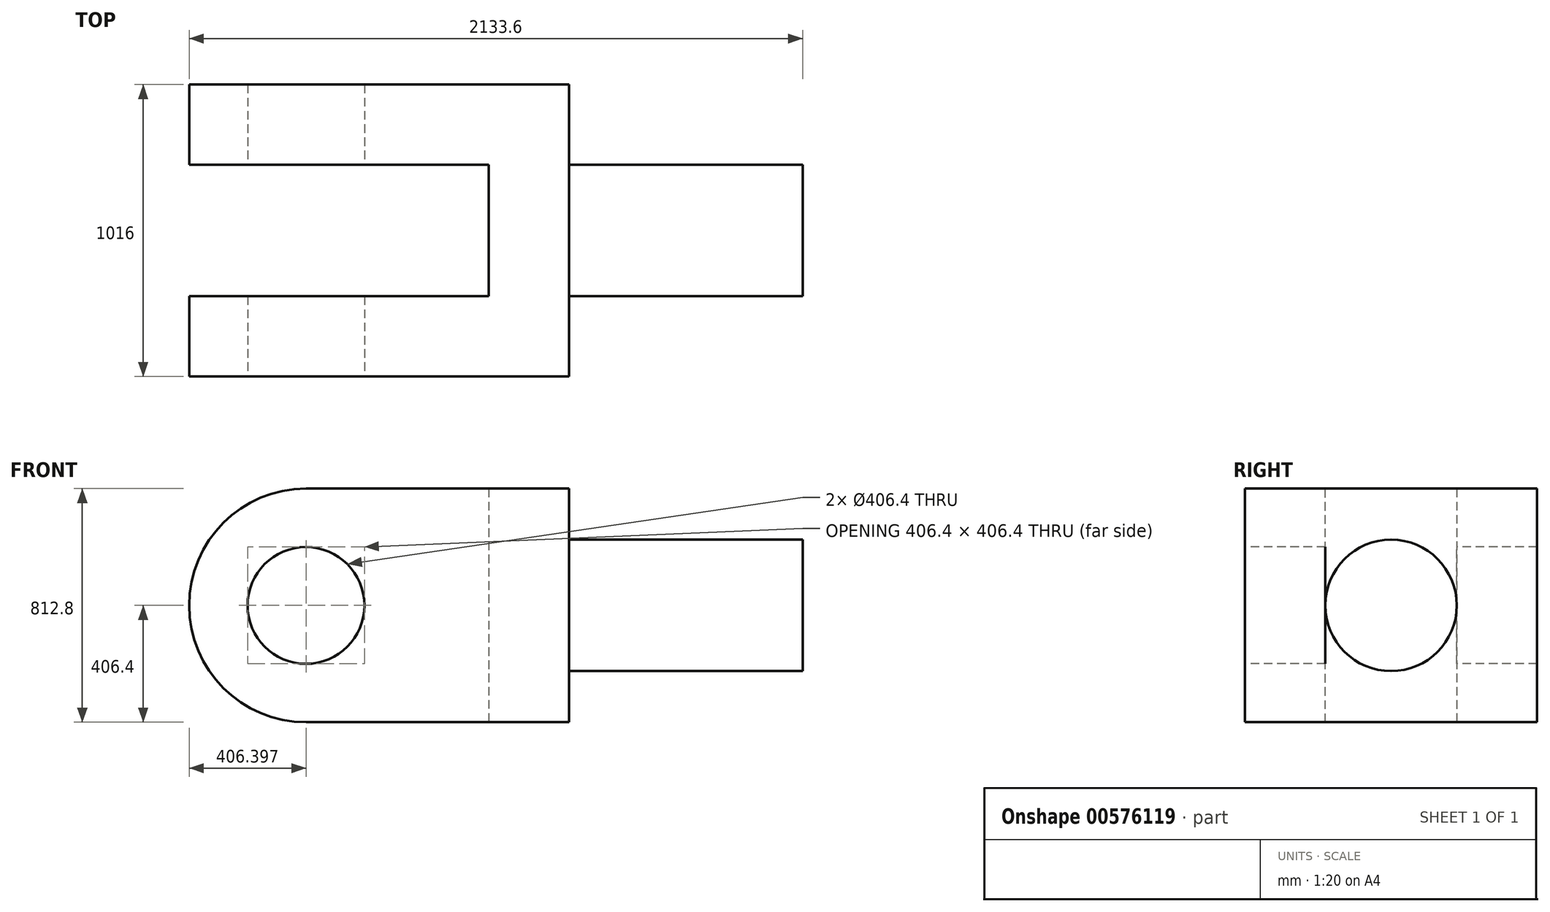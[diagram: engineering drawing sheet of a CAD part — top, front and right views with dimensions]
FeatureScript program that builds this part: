
annotation { "Feature Type Name" : "Feature", "Feature Type Description" : "" }
export const myFeature = defineFeature(function(context is Context, id is Id, definition is map)
    precondition{}
    {
        {
            var Q0;
            Q0=qCreatedBy(makeId("Top.planeOp"),FACE);
            var sketch = newSketch(context, id + "F0", { "sketchPlane" : qUnion([Q0])});
            skLineSegment(sketch, "E0", {"start": v(-50.28, 38.46) * mm, "end": v(1270.52, 38.46) * mm});
            skLineSegment(sketch, "E1", {"start": v(1270.52, 38.46) * mm, "end": v(1270.52, -977.54) * mm});
            skLineSegment(sketch, "E2", {"start": v(1270.52, -977.54) * mm, "end": v(-50.28, -977.54) * mm});
            skLineSegment(sketch, "E3", {"start": v(-50.28, -977.54) * mm, "end": v(-50.28, -698.14) * mm});
            skLineSegment(sketch, "E4", {"start": v(-50.28, -698.14) * mm, "end": v(991.12, -698.14) * mm});
            skLineSegment(sketch, "E5", {"start": v(991.12, -698.14) * mm, "end": v(991.12, -240.94) * mm});
            skLineSegment(sketch, "E6", {"start": v(991.12, -240.94) * mm, "end": v(-50.28, -240.94) * mm});
            skLineSegment(sketch, "E7", {"start": v(-50.28, -240.94) * mm, "end": v(-50.28, 38.46) * mm});
            skSolve(sketch);
        }
        {
            var Q0;
            Q0 = qSketchRegion(id + "F0", true);
            extrude(context, id + "F1", {"entities" : qUnion([Q0]), "depth" : 812.8 * mm, "offsetDistance" : 25.4 * mm});
        }
        {
            var Q0;
            Q0=makeQuery(id+"F1.opExtrude","SWEPT_FACE",FACE,{"disambiguationData":[OSD([sQuery(id+"F0.wireOp",EDGE,"E0")])]});
            var sketch = newSketch(context, id + "F2", { "sketchPlane" : qUnion([Q0])});
            skLineSegment(sketch, "E8", {"start": v(50.28, 812.8) * mm, "end": v(-356.12, 812.8) * mm});
            skPoint(sketch, "E9.centerSnap0", {"position": v(50.28, 406.4) * mm});
            skLineSegment(sketch, "E10", {"start": v(50.28, 0) * mm, "end": v(-356.12, 0) * mm});
            skArc(sketch, "E11", {"start": v(-356.12, 0) * mm, "mid": v(50.28, 406.4) * mm, "end": v(-356.12, 812.8) * mm});
            skSolve(sketch);
        }
        {
            var Q0;
            {var subQ0=sQuery(id+"F2.wireOp",EDGE,"E8");Q0=makeQuery(id+"F2.imprint","IMPRINT",FACE,{"disambiguationData":[TD([[makeQuery(id+"F2.imprint","IMPRINT",EDGE,{"derivedFrom":subQ0}),1.0]])]});}
            var Q1;
            {var subQ0=sQuery(id+"F2.wireOp",EDGE,"E10");Q1=makeQuery(id+"F2.imprint","IMPRINT",FACE,{"disambiguationData":[TD([[makeQuery(id+"F2.imprint","IMPRINT",EDGE,{"derivedFrom":subQ0}),-1.0]])]});}
            extrude(context, id + "F3", {"entities" : qUnion([Q0, Q1]), "operationType" : NewBodyOperationType.REMOVE, "endBound" : BoundingType.THROUGH_ALL, "oppositeDirection" : true, "depth" : 25.4 * mm, "offsetDistance" : 25.4 * mm});
        }
        {
            var Q0;
            Q0=makeQuery(id+"F1.opExtrude","CAP_FACE",FACE,{"disambiguationData":[OSD([sQuery(id+"F0.wireOp",EDGE,"E0"),sQuery(id+"F0.wireOp",EDGE,"E1"),sQuery(id+"F0.wireOp",EDGE,"E2"),sQuery(id+"F0.wireOp",EDGE,"E3"),sQuery(id+"F0.wireOp",EDGE,"E4"),sQuery(id+"F0.wireOp",EDGE,"E5"),sQuery(id+"F0.wireOp",EDGE,"E6"),sQuery(id+"F0.wireOp",EDGE,"E7")])],"isStart":false});
            var sketch = newSketch(context, id + "F4", { "sketchPlane" : qUnion([Q0])});
            skLineSegment(sketch, "E12", {"start": v(1270.52, -977.54) * mm, "end": v(1270.52, -698.14) * mm});
            skLineSegment(sketch, "E13", {"start": v(1270.52, -698.14) * mm, "end": v(2083.32, -698.14) * mm});
            skLineSegment(sketch, "E14", {"start": v(2083.32, -698.14) * mm, "end": v(2083.32, -240.94) * mm});
            skLineSegment(sketch, "E15", {"start": v(2083.32, -240.94) * mm, "end": v(1270.52, -240.94) * mm});
            skSolve(sketch);
        }
        {
            var Q0;
            {var subQ0=sQuery(id+"F4.wireOp",EDGE,"E13");Q0=makeQuery(id+"F4.imprint","IMPRINT",FACE,{"disambiguationData":[TD([[makeQuery(id+"F4.imprint","IMPRINT",EDGE,{"derivedFrom":subQ0}),1.0]])]});}
            extrude(context, id + "F5", {"entities" : qUnion([Q0]), "operationType" : NewBodyOperationType.ADD, "oppositeDirection" : true, "depth" : 812.8 * mm, "offsetDistance" : 25.4 * mm});
        }
        {
            var Q0;
            Q0=makeQuery(id+"F5.opExtrude","SWEPT_FACE",FACE,{"disambiguationData":[OSD([sQuery(id+"F4.wireOp",EDGE,"E14")])]});
            var sketch = newSketch(context, id + "F6", { "sketchPlane" : qUnion([Q0])});
            skCircle(sketch, "E16", {"center": v(-469.54, 406.4) * mm, "radius": 228.6 * mm});
            skPoint(sketch, "E16.centerSnap0", {"position": v(-698.14, 406.4) * mm});
            skPoint(sketch, "E16.centerSnap1", {"position": v(-469.54, 0) * mm});
            skSolve(sketch);
        }
        {
            var Q0;
            {var subQ1=sQuery(id+"F4.wireOp",EDGE,"E14");var subQ6=makeQuery(id+"F5.opExtrude","CAP_EDGE",EDGE,{"disambiguationData":[OSD([subQ1])],"isStart":true});Q0=makeQuery(id+"F6.imprint","IMPRINT",FACE,{"disambiguationData":[TD([[makeQuery(id+"F6.imprint","IMPRINT",EDGE,{"derivedFrom":subQ6}),-1.0]])]});}
            var Q1;
            {var subQ1=sQuery(id+"F4.wireOp",EDGE,"E14");var subQ6=makeQuery(id+"F5.opExtrude","CAP_EDGE",EDGE,{"disambiguationData":[OSD([subQ1])],"isStart":false});Q1=makeQuery(id+"F6.imprint","IMPRINT",FACE,{"disambiguationData":[TD([[makeQuery(id+"F6.imprint","IMPRINT",EDGE,{"derivedFrom":subQ6}),1.0]])]});}
            extrude(context, id + "F7", {"entities" : qUnion([Q0, Q1]), "operationType" : NewBodyOperationType.REMOVE, "oppositeDirection" : true, "depth" : 812.8 * mm, "offsetDistance" : 25.4 * mm});
        }
        {
            var Q0;
            Q0=makeQuery(id+"F1.opExtrude","SWEPT_FACE",FACE,{"disambiguationData":[OSD([sQuery(id+"F0.wireOp",EDGE,"E2")])]});
            var sketch = newSketch(context, id + "F8", { "sketchPlane" : qUnion([Q0])});
            skCircle(sketch, "E17", {"center": v(356.12, 406.4) * mm, "radius": 203.2 * mm});
            skSolve(sketch);
        }
        {
            var Q0;
            Q0=makeQuery(id+"F8.imprint","IMPRINT",FACE,{"disambiguationData":[TD([[makeQuery(id+"F8.imprint","IMPRINT",EDGE,{"derivedFrom":sQuery(id+"F8.wireOp",EDGE,"E17")}),1.0]])]});
            extrude(context, id + "F9", {"entities" : qUnion([Q0]), "operationType" : NewBodyOperationType.REMOVE, "endBound" : BoundingType.THROUGH_ALL, "oppositeDirection" : true, "depth" : 25.4 * mm, "offsetDistance" : 25.4 * mm});
        }
    });
